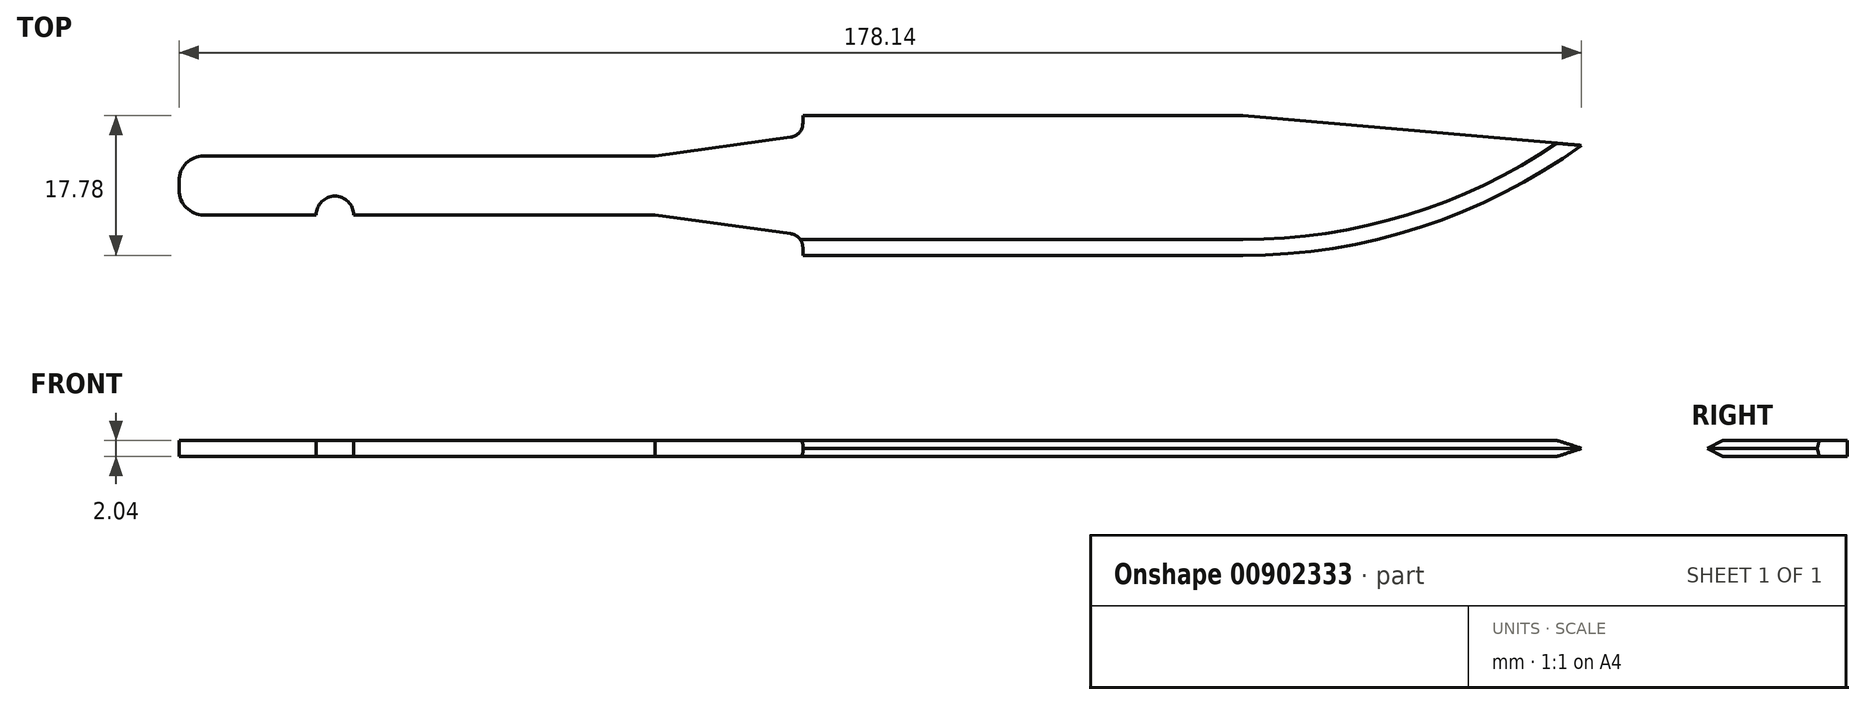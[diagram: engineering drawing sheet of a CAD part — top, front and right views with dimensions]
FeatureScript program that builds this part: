
annotation { "Feature Type Name" : "Feature", "Feature Type Description" : "" }
export const myFeature = defineFeature(function(context is Context, id is Id, definition is map)
    precondition{}
    {
        {
            var Q0;
            Q0=qCreatedBy(makeId("Top.planeOp"),FACE);
            var sketch = newSketch(context, id + "F0", { "sketchPlane" : qUnion([Q0])});
            skLineSegment(sketch, "E0", {"start": v(34.3, 24.07) * mm, "end": v(34.3, 16.57) * mm, "construction": true});
            skLineSegment(sketch, "E1", {"start": v(34.3, 24.07) * mm, "end": v(51.55, 26.46) * mm});
            skLineSegment(sketch, "E2", {"start": v(53.09, 28.22) * mm, "end": v(53.09, 29.2) * mm});
            skLineSegment(sketch, "E3", {"start": v(53.09, 29.2) * mm, "end": v(59.44, 29.2) * mm});
            skLineSegment(sketch, "E4", {"start": v(59.44, 29.2) * mm, "end": v(59.44, 11.43) * mm, "construction": true});
            skLineSegment(sketch, "E5", {"start": v(59.44, 11.43) * mm, "end": v(53.09, 11.43) * mm});
            skLineSegment(sketch, "E6", {"start": v(53.09, 11.43) * mm, "end": v(53.09, 12.42) * mm});
            skLineSegment(sketch, "E7", {"start": v(51.55, 14.18) * mm, "end": v(34.3, 16.57) * mm});
            skPoint(sketch, "E8.visualSharp", {"position": v(53.09, 13.97) * mm});
            skArc(sketch, "E8.filletArc", {"start": v(53.09, 12.42) * mm, "mid": v(52.65, 13.59) * mm, "end": v(51.55, 14.18) * mm});
            skPoint(sketch, "E9.visualSharp", {"position": v(53.09, 26.67) * mm});
            skArc(sketch, "E9.filletArc", {"start": v(51.55, 26.46) * mm, "mid": v(52.65, 27.05) * mm, "end": v(53.09, 28.22) * mm});
            skLineSegment(sketch, "E10", {"start": v(0, 20.32) * mm, "end": v(59.44, 20.32) * mm, "construction": true});
            skPoint(sketch, "E11", {"position": v(34.3, 20.32) * mm});
            skLineSegment(sketch, "E12", {"start": v(34.3, 16.57) * mm, "end": v(-3.97, 16.57) * mm});
            skLineSegment(sketch, "E13", {"start": v(34.3, 24.07) * mm, "end": v(-22.99, 24.07) * mm});
            skLineSegment(sketch, "E14", {"start": v(-26.16, 20.9) * mm, "end": v(-26.16, 19.75) * mm});
            skArc(sketch, "E15", {"start": v(-3.97, 16.57) * mm, "mid": v(-6.35, 18.95) * mm, "end": v(-8.73, 16.57) * mm});
            skLineSegment(sketch, "E16.trimOffspring", {"start": v(-8.73, 16.57) * mm, "end": v(-22.99, 16.57) * mm});
            skPoint(sketch, "E17.visualSharp", {"position": v(-26.16, 24.07) * mm});
            skArc(sketch, "E17.filletArc", {"start": v(-22.99, 24.07) * mm, "mid": v(-25.23, 23.14) * mm, "end": v(-26.16, 20.9) * mm});
            skPoint(sketch, "E18.visualSharp", {"position": v(-26.16, 16.57) * mm});
            skArc(sketch, "E18.filletArc", {"start": v(-26.16, 19.75) * mm, "mid": v(-25.23, 17.5) * mm, "end": v(-22.99, 16.57) * mm});
            skLineSegment(sketch, "E19", {"start": v(59.44, 29.2) * mm, "end": v(108.97, 29.2) * mm});
            skLineSegment(sketch, "E20", {"start": v(108.97, 29.21) * mm, "end": v(151.98, 25.4) * mm});
            skLineSegment(sketch, "E21", {"start": v(59.44, 11.43) * mm, "end": v(108.97, 11.43) * mm});
            skArc(sketch, "E22", {"start": v(108.97, 11.43) * mm, "mid": v(131.58, 15.01) * mm, "end": v(151.98, 25.4) * mm});
            skSolve(sketch);
        }
        {
            var Q0;
            Q0=qSketchRegion(id+"F0",true);
            extrude(context, id + "F1", {"entities" : qUnion([Q0]), "endBound" : BoundingType.SYMMETRIC, "depth" : 2.03 * mm, "offsetDistance" : 25.4 * mm});
        }
        {
            var Q0;
            Q0=makeQuery(id+"F1.opExtrude","CAP_EDGE",EDGE,{"disambiguationData":[OSD([sQuery(id+"F0.wireOp",EDGE,"E5"),sQuery(id+"F0.wireOp",EDGE,"E21")])],"isStart":false});
            chamfer(context, id + "F2", {"entities" : qUnion([Q0]), "chamferType" : ChamferType.TWO_OFFSETS, "width1" : 1 * mm, "oppositeDirection" : false, "width2" : 2 * mm, "tangentPropagation" : true});
        }
        {
            var Q0;
            Q0=makeQuery(id+"F1.opExtrude","CAP_EDGE",EDGE,{"disambiguationData":[OSD([sQuery(id+"F0.wireOp",EDGE,"E5"),sQuery(id+"F0.wireOp",EDGE,"E21")])],"isStart":true});
            chamfer(context, id + "F3", {"entities" : qUnion([Q0]), "chamferType" : ChamferType.TWO_OFFSETS, "width1" : 2 * mm, "oppositeDirection" : false, "width2" : 1 * mm, "tangentPropagation" : true});
        }
    });
